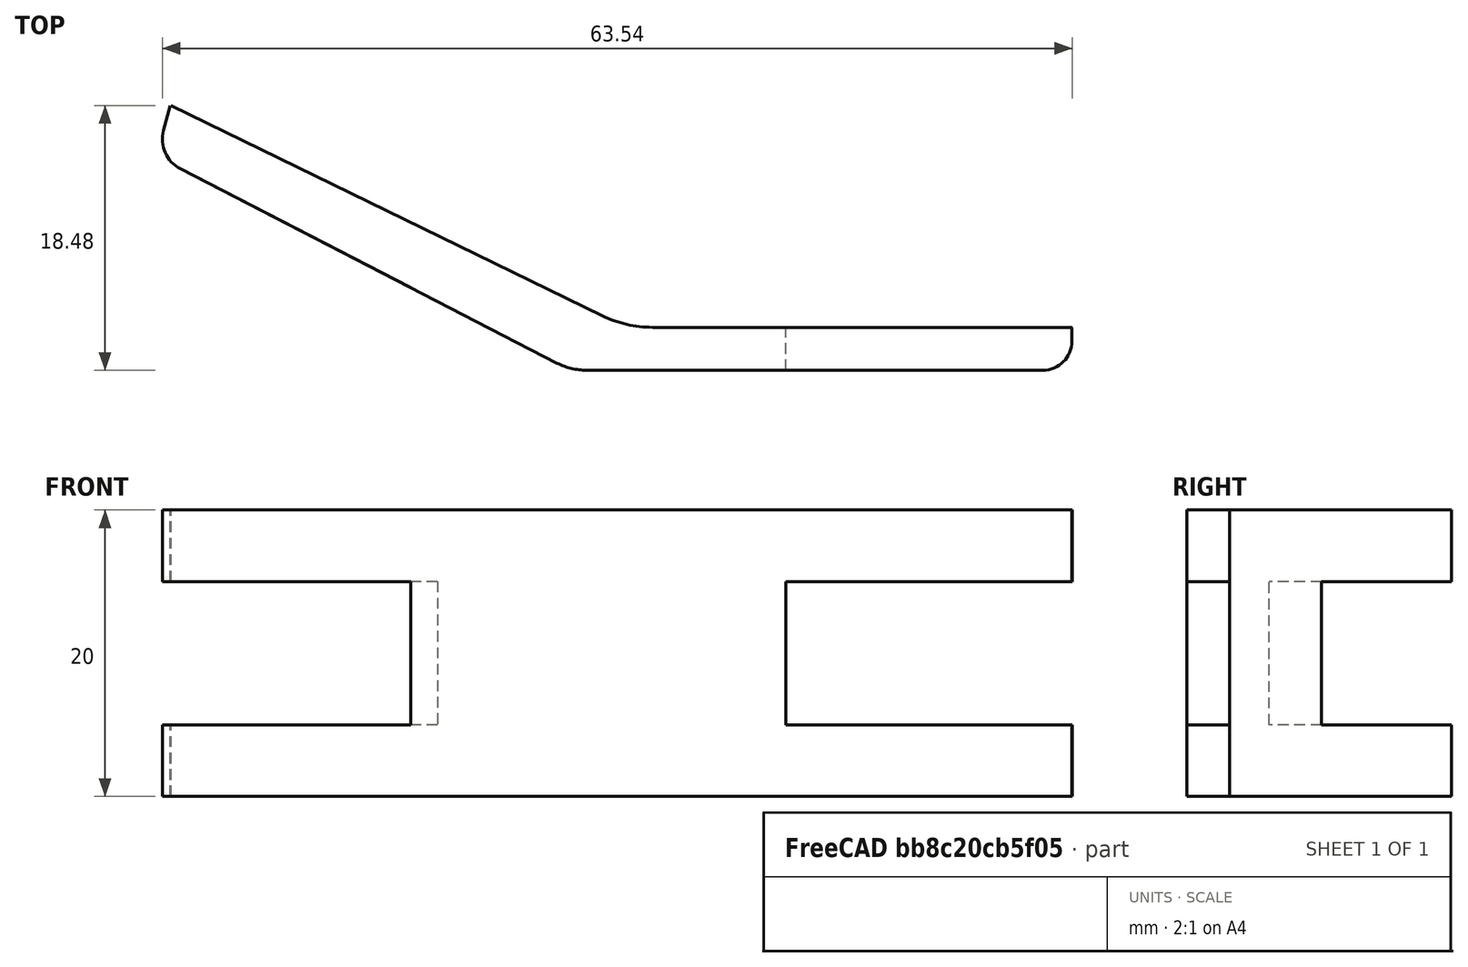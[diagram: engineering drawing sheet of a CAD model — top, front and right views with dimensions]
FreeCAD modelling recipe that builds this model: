
FCSTD DOCUMENT
Label: j-support_v0
objects: Part::Box×2, Sketcher::SketchObject×1, PartDesign::Pad×1, Part::Cut×1, Part::Fuse×1
note: 7 computed .brp shape members not serialized (recipe doc carries the construction recipe); baked Part::Feature solids carry a one-line shape summary decoded from their .brp

FEATURE [Sketcher::SketchObject] Sketch
  sketch-geometry (10):
    g0: LineSegment StartX=1.07418 StartY=0 StartZ=0 EndX=32.9556 EndY=0 EndZ=0
    g1: LineSegment StartX=-0.954606 StartY=0.492526 StartZ=0 EndX=-27.2727 EndY=14.0713 EndZ=0
    g2: LineSegment StartX=34.9766 StartY=2.02108 StartZ=0 EndX=34.9766 EndY=3 EndZ=0
    g3: LineSegment StartX=35 StartY=3 StartZ=0 EndX=5.68568 EndY=3 EndZ=0
    g4: LineSegment StartX=-28.4571 StartY=16.7472 StartZ=0 EndX=-27.9958 EndY=18.4736 EndZ=0
    g5: LineSegment StartX=-27.9147 StartY=18.4751 StartZ=0 EndX=2.17612 EndY=3.8097 EndZ=0
    g6: ArcOfCircle CenterX=5.68568 CenterY=11.0107 CenterZ=0 NormalX=0 NormalY=0 NormalZ=1 Radius=8.01071 StartAngle=4.2589 EndAngle=4.71239
    g7: ArcOfCircle CenterX=32.9556 CenterY=2.02108 CenterZ=0 NormalX=0 NormalY=0 NormalZ=1 Radius=2.02108 StartAngle=4.71239 EndAngle=6.28319
    g8: ArcOfCircle CenterX=-26.2028 CenterY=16.1449 CenterZ=0 NormalX=0 NormalY=0 NormalZ=1 Radius=2.33338 StartAngle=2.8805 EndAngle=4.23607
    g9: ArcOfCircle CenterX=1.07418 CenterY=4.42468 CenterZ=0 NormalX=0 NormalY=0 NormalZ=1 Radius=4.42468 StartAngle=4.23607 EndAngle=4.71239
  constraints (11):
    c: Horizontal(g0)
    c: Vertical(g2)
    c: Horizontal(g3)
    c: Tangent(g5,g6)
    c: Tangent(g3,g6)
    c: Tangent(g0,g7)
    c: Tangent(g2,g7)
    c: Tangent(g1,g8)
    c: Tangent(g4,g8)
    c: Tangent(g1,g9)
    c: Tangent(g0,g9)
FEATURE [PartDesign::Pad] Pad
  Length = 20
  Length2 = 100
  Sketch = -> Sketch
  Type = 0
FEATURE [Part::Box] Box
  Height = 10
  Length = 25
  Placement = pos=(15,-3,5) rot=(0,0,1;0rad)
  Width = 10
FEATURE [Part::Box] Box001
  Height = 10
  Length = 25
  Placement = pos=(-8,12,5) rot=(0,0,1;2.67035rad)
  Width = 10
FEATURE [Part::Cut] Cut
  Base = -> Pad
  Tool = -> Box
FEATURE [Part::Fuse] Fusion
  Base = -> Box001
  Tool = -> Cut
